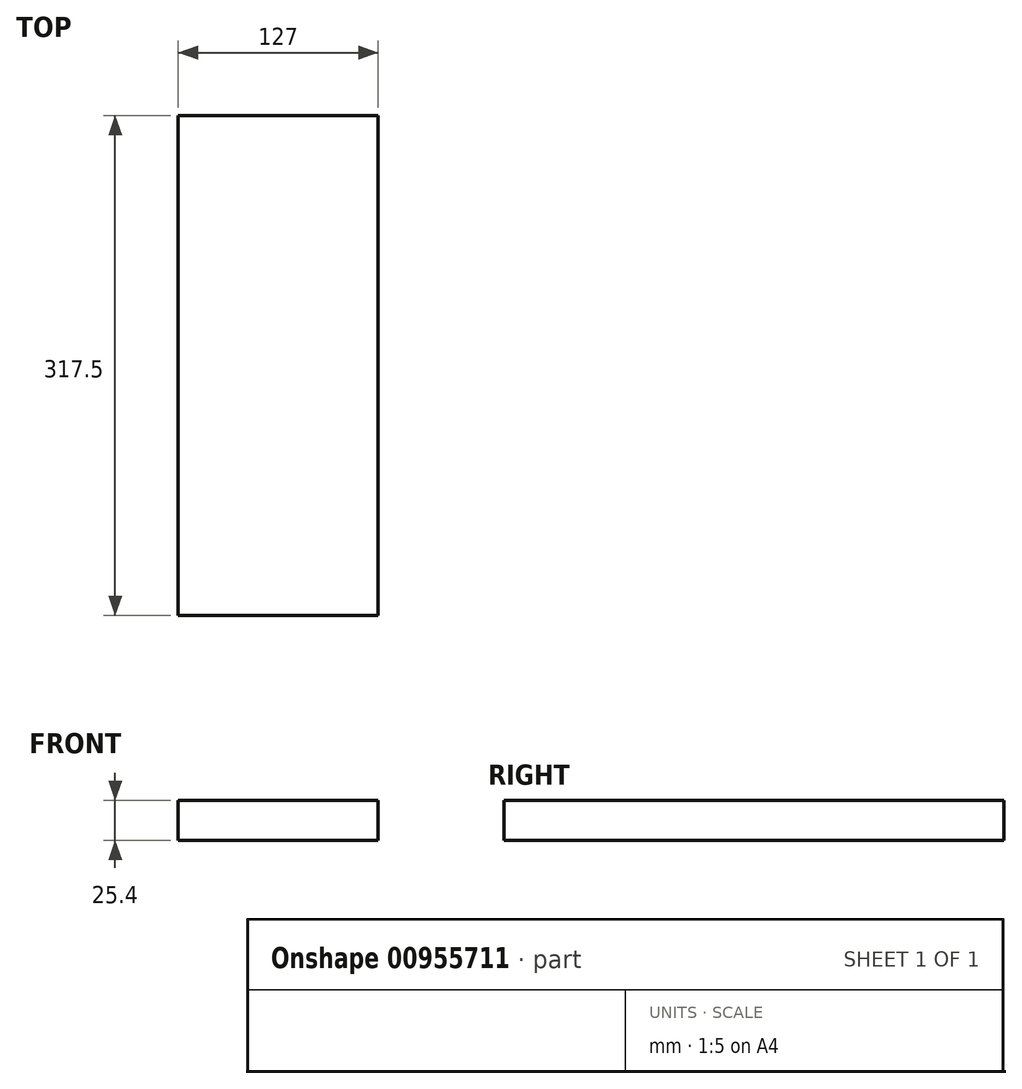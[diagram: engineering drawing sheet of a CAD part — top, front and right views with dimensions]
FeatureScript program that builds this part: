
annotation { "Feature Type Name" : "Feature", "Feature Type Description" : "" }
export const myFeature = defineFeature(function(context is Context, id is Id, definition is map)
    precondition{}
    {
        {
            var Q0;
            Q0=qCreatedBy(makeId("Top.planeOp"),FACE);
            var sketch = newSketch(context, id + "F0", { "sketchPlane" : qUnion([Q0])});
            skLineSegment(sketch, "E0.bottom", {"start": v(63.5, -158.75) * mm, "end": v(-63.5, -158.75) * mm});
            skLineSegment(sketch, "E0.top", {"start": v(63.5, 158.75) * mm, "end": v(-63.5, 158.75) * mm});
            skLineSegment(sketch, "E0.left", {"start": v(63.5, -158.75) * mm, "end": v(63.5, 158.75) * mm});
            skLineSegment(sketch, "E0.right", {"start": v(-63.5, -158.75) * mm, "end": v(-63.5, 158.75) * mm});
            skPoint(sketch, "E0.middle", {"position": v(0, 0) * mm});
            skSolve(sketch);
        }
        {
            var Q0;
            Q0 = qSketchRegion(id + "F0", true);
            extrude(context, id + "F1", {"entities" : qUnion([Q0]), "depth" : 25.4 * mm, "offsetDistance" : 25.4 * mm});
        }
    });
